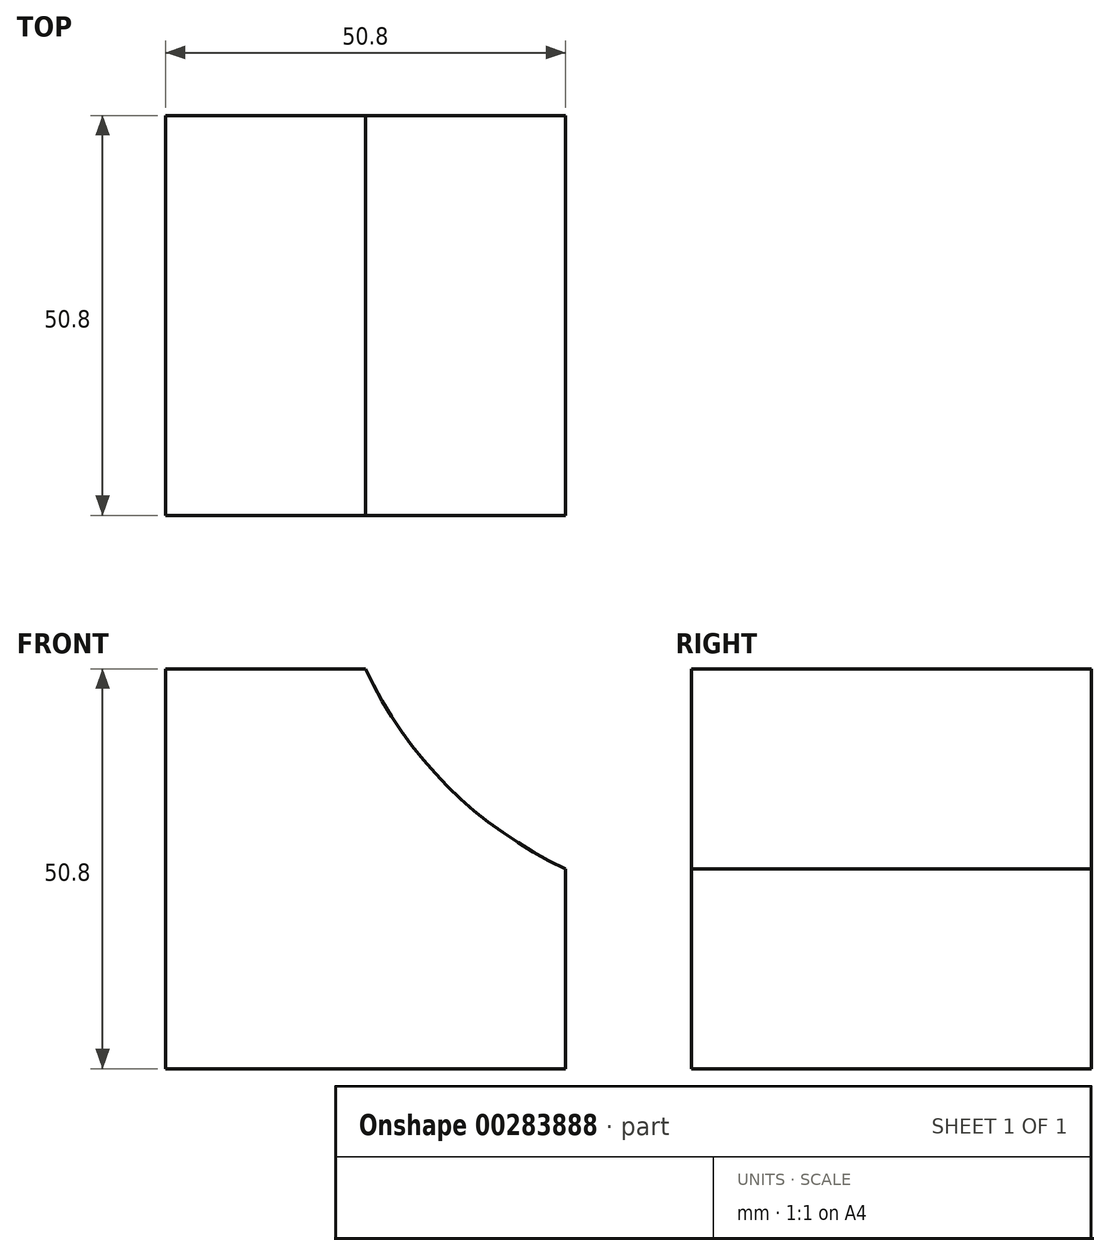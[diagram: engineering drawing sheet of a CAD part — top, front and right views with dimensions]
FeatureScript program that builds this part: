
annotation { "Feature Type Name" : "Feature", "Feature Type Description" : "" }
export const myFeature = defineFeature(function(context is Context, id is Id, definition is map)
    precondition{}
    {
        {
            var Q0;
            Q0=qCreatedBy(makeId("Front.planeOp"),FACE);
            var sketch = newSketch(context, id + "F0", { "sketchPlane" : qUnion([Q0])});
            skLineSegment(sketch, "E0", {"start": v(0, 0) * mm, "end": v(-50.8, 0) * mm});
            skLineSegment(sketch, "E1", {"start": v(-50.8, 0) * mm, "end": v(-50.8, 50.8) * mm});
            skLineSegment(sketch, "E2", {"start": v(-50.8, 50.8) * mm, "end": v(-25.4, 50.8) * mm});
            skLineSegment(sketch, "E3", {"start": v(0, 0) * mm, "end": v(0, 25.4) * mm});
            skArc(sketch, "E4", {"start": v(-25.4, 50.8) * mm, "mid": v(-14.96, 35.84) * mm, "end": v(0, 25.4) * mm});
            skSolve(sketch);
        }
        {
            var Q0;
            Q0=makeQuery(id+"F0.imprint","IMPRINT",FACE,{"disambiguationData":[TD([[makeQuery(id+"F0.imprint","IMPRINT",EDGE,{"derivedFrom":sQuery(id+"F0.wireOp",EDGE,"E0")}),-1.0]])]});
            extrude(context, id + "F1", {"entities" : qUnion([Q0]), "depth" : 50.8 * mm});
        }
    });
